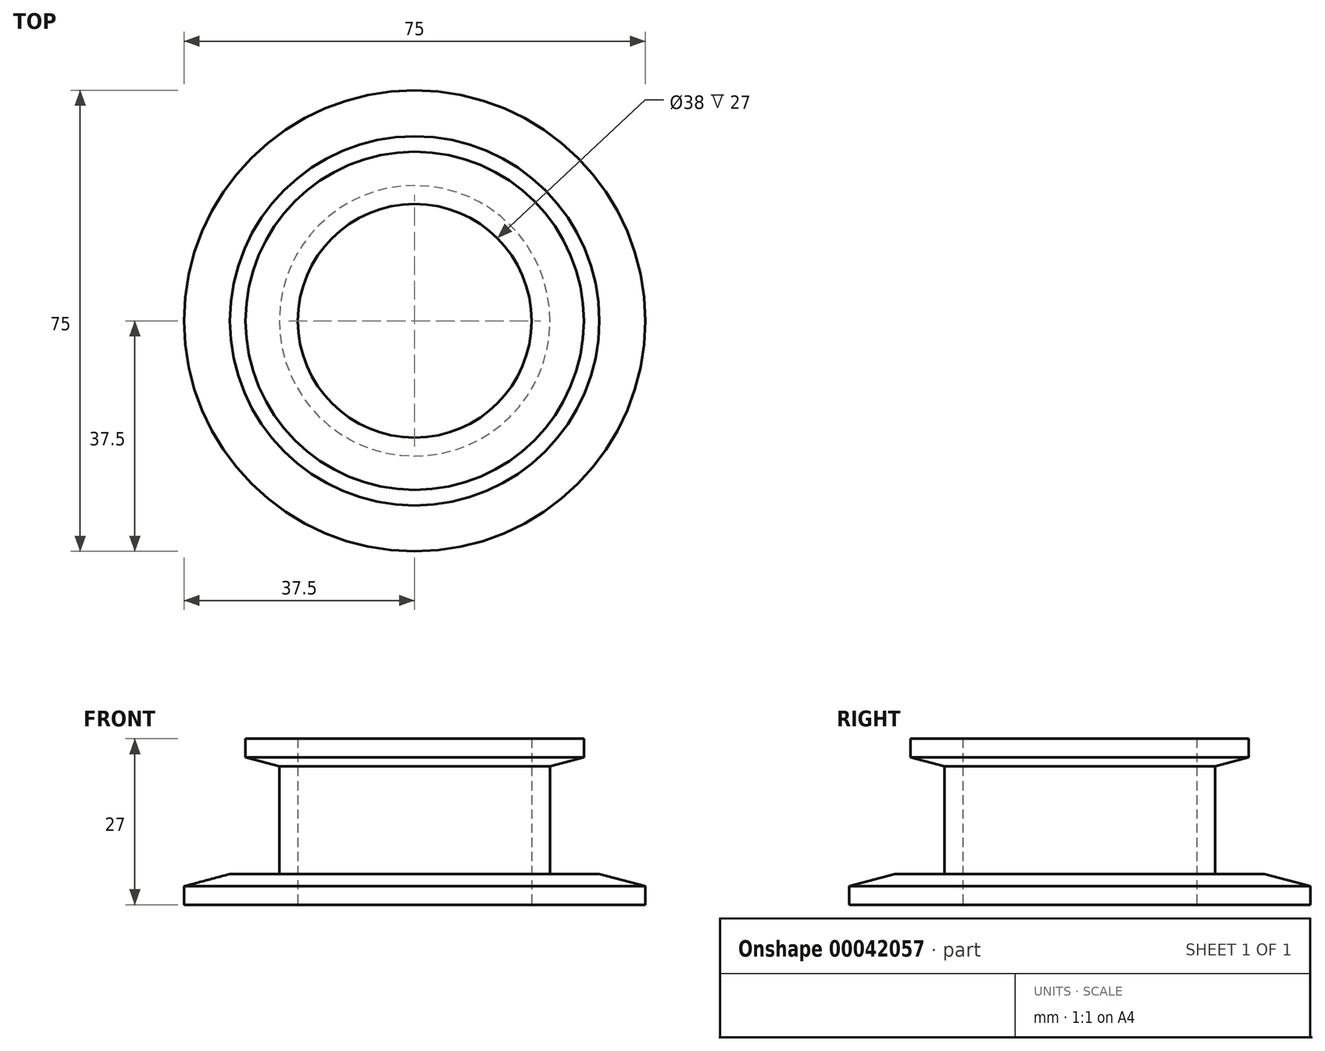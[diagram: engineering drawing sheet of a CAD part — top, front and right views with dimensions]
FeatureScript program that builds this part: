
annotation { "Feature Type Name" : "Feature", "Feature Type Description" : "" }
export const myFeature = defineFeature(function(context is Context, id is Id, definition is map)
    precondition{}
    {
        {
            var Q0;
            Q0=qCreatedBy(makeId("Front.planeOp"),FACE);
            var sketch = newSketch(context, id + "F0", { "sketchPlane" : qUnion([Q0])});
            skLineSegment(sketch, "E0", {"start": v(0, 0) * mm, "end": v(0, 27) * mm, "construction": true});
            skLineSegment(sketch, "E1", {"start": v(19, 0) * mm, "end": v(19, 27) * mm});
            skLineSegment(sketch, "E2", {"start": v(19, 0) * mm, "end": v(37.5, 0) * mm});
            skLineSegment(sketch, "E3", {"start": v(37.5, 0) * mm, "end": v(37.5, 3) * mm});
            skLineSegment(sketch, "E4", {"start": v(37.5, 3) * mm, "end": v(30.04, 5) * mm});
            skLineSegment(sketch, "E5", {"start": v(30.04, 5) * mm, "end": v(22, 5) * mm});
            skLineSegment(sketch, "E6", {"start": v(22, 5) * mm, "end": v(22, 22.53) * mm});
            skLineSegment(sketch, "E7", {"start": v(22, 22.53) * mm, "end": v(27.5, 24) * mm});
            skLineSegment(sketch, "E8", {"start": v(27.5, 24) * mm, "end": v(27.5, 27) * mm});
            skLineSegment(sketch, "E9", {"start": v(27.5, 27) * mm, "end": v(19, 27) * mm});
            skSolve(sketch);
        }
        {
            var Q0;
            Q0=makeQuery(id+"F0.imprint","IMPRINT",FACE,{"disambiguationData":[TD([[makeQuery(id+"F0.imprint","IMPRINT",EDGE,{"derivedFrom":sQuery(id+"F0.wireOp",EDGE,"E1")}),-1.0]])]});
            var Q1;
            Q1=sQuery(id+"F0.wireOp",EDGE,"E0");
            revolve(context, id + "F1", {"entities" : qUnion([Q0]), "axis" : qUnion([Q1]), "revolveType" : RevolveType.FULL});
        }
    });
